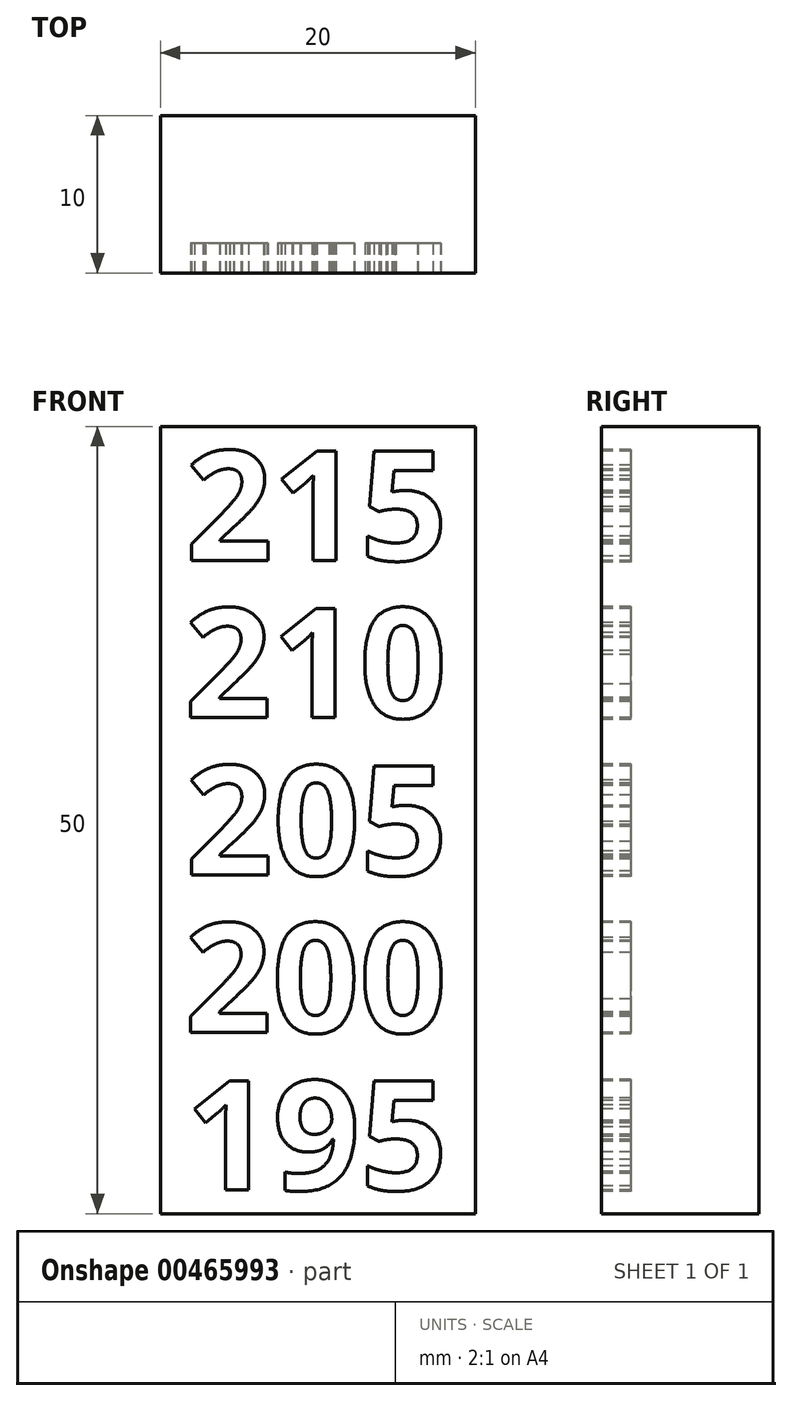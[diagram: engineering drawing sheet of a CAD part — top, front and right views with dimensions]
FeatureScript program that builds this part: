
annotation { "Feature Type Name" : "Feature", "Feature Type Description" : "" }
export const myFeature = defineFeature(function(context is Context, id is Id, definition is map)
    precondition{}
    {
        {
            var Q0;
            Q0=qCreatedBy(makeId("Top.planeOp"),FACE);
            var sketch = newSketch(context, id + "F0", { "sketchPlane" : qUnion([Q0])});
            skLineSegment(sketch, "E0.bottom", {"start": v(10, -5) * mm, "end": v(-10, -5) * mm});
            skLineSegment(sketch, "E0.top", {"start": v(10, 5) * mm, "end": v(-10, 5) * mm});
            skLineSegment(sketch, "E0.left", {"start": v(10, -5) * mm, "end": v(10, 5) * mm});
            skLineSegment(sketch, "E0.right", {"start": v(-10, -5) * mm, "end": v(-10, 5) * mm});
            skPoint(sketch, "E0.middle", {"position": v(0, 0) * mm});
            skSolve(sketch);
        }
        {
            var Q0;
            Q0=makeQuery(id+"F0.imprint","IMPRINT",FACE,{"disambiguationData":[TD([[makeQuery(id+"F0.imprint","IMPRINT",EDGE,{"derivedFrom":sQuery(id+"F0.wireOp",EDGE,"E0.bottom")}),-1.0]])]});
            extrude(context, id + "F1", {"entities" : qUnion([Q0]), "depth" : 50 * mm});
        }
        {
            var Q0;
            Q0=makeQuery(id+"F1.opExtrude","SWEPT_FACE",FACE,{"disambiguationData":[OSD([sQuery(id+"F0.wireOp",EDGE,"E0.bottom")])]});
            var sketch = newSketch(context, id + "F2", { "sketchPlane" : qUnion([Q0])});
            skLineSegment(sketch, "E1.bottom", {"start": v(-10, 50) * mm, "end": v(10, 50) * mm});
            skLineSegment(sketch, "E1.top", {"start": v(-10, 40) * mm, "end": v(10, 40) * mm});
            skLineSegment(sketch, "E1.left", {"start": v(-10, 50) * mm, "end": v(-10, 40) * mm});
            skLineSegment(sketch, "E1.right", {"start": v(10, 50) * mm, "end": v(10, 40) * mm});
            skLineSegment(sketch, "E2.bottom", {"start": v(10, 40) * mm, "end": v(-10, 40) * mm});
            skLineSegment(sketch, "E2.top", {"start": v(10, 30) * mm, "end": v(-10, 30) * mm});
            skLineSegment(sketch, "E2.left", {"start": v(10, 40) * mm, "end": v(10, 30) * mm});
            skLineSegment(sketch, "E2.right", {"start": v(-10, 40) * mm, "end": v(-10, 30) * mm});
            skLineSegment(sketch, "E3.bottom", {"start": v(-10, 30) * mm, "end": v(10, 30) * mm});
            skLineSegment(sketch, "E3.top", {"start": v(-10, 20) * mm, "end": v(10, 20) * mm});
            skLineSegment(sketch, "E3.left", {"start": v(-10, 30) * mm, "end": v(-10, 20) * mm});
            skLineSegment(sketch, "E3.right", {"start": v(10, 30) * mm, "end": v(10, 20) * mm});
            skLineSegment(sketch, "E4.bottom", {"start": v(10, 20) * mm, "end": v(-10, 20) * mm});
            skLineSegment(sketch, "E4.top", {"start": v(10, 10) * mm, "end": v(-10, 10) * mm});
            skLineSegment(sketch, "E4.left", {"start": v(10, 20) * mm, "end": v(10, 10) * mm});
            skLineSegment(sketch, "E4.right", {"start": v(-10, 20) * mm, "end": v(-10, 10) * mm});
            skLineSegment(sketch, "E5.bottom", {"start": v(-10, 10) * mm, "end": v(10, 10) * mm});
            skLineSegment(sketch, "E5.top", {"start": v(-10, 0) * mm, "end": v(10, 0) * mm});
            skLineSegment(sketch, "E5.left", {"start": v(-10, 10) * mm, "end": v(-10, 0) * mm});
            skLineSegment(sketch, "E5.right", {"start": v(10, 10) * mm, "end": v(10, 0) * mm});
            skPoint(sketch, "E6", {"position": v(0, 5) * mm});
            skPoint(sketch, "E7", {"position": v(0, 15) * mm});
            skPoint(sketch, "E8", {"position": v(0, 25) * mm});
            skPoint(sketch, "E9", {"position": v(0, 35) * mm});
            skPoint(sketch, "E10", {"position": v(0, 45) * mm});
            skLineSegment(sketch, "E11", {"start": v(-10, 45) * mm, "end": v(10, 45) * mm, "construction": true});
            skLineSegment(sketch, "E12", {"start": v(10, 35) * mm, "end": v(-10, 35) * mm, "construction": true});
            skLineSegment(sketch, "E13", {"start": v(-10, 25) * mm, "end": v(10, 25) * mm, "construction": true});
            skLineSegment(sketch, "E14", {"start": v(10, 15) * mm, "end": v(-10, 15) * mm, "construction": true});
            skLineSegment(sketch, "E15", {"start": v(-10, 5) * mm, "end": v(10, 5) * mm, "construction": true});
            skText(sketch, "E16", { "text": "195", "fontName": "OpenSans-Bold.ttf"});
            skText(sketch, "E17", { "text": "200", "fontName": "OpenSans-Bold.ttf"});
            skText(sketch, "E18", { "text": "210", "fontName": "OpenSans-Bold.ttf"});
            skText(sketch, "E19", { "text": "205", "fontName": "OpenSans-Bold.ttf"});
            skText(sketch, "E20", { "text": "215", "fontName": "OpenSans-Bold.ttf"});
            const initialGuessF2  = {"E16": [-0.00842, 0.0015, 1, 0, 0.007], "E17": [-0.00847, 0.0115, 1, 0, 0.007], "E18": [-0.00847, 0.0315, 1, 0, 0.007], "E19": [-0.00842, 0.0215, 1, 0, 0.007], "E20": [-0.00842, 0.0415, 1, 0, 0.007]};
            skSetInitialGuess(sketch, initialGuessF2);
            skSolve(sketch);
        }
        {
            var Q0;
            Q0=makeQuery(id+"F2.imprint","IMPRINT",FACE,{"disambiguationData":[TD([[makeQuery(id+"F2.imprint","IMPRINT",EDGE,{"derivedFrom":sQuery(id+"F2.wireOp",EDGE,"E20.sketch_text.stroke-0")}),-1.0]])]});
            var Q1;
            Q1=makeQuery(id+"F2.imprint","IMPRINT",FACE,{"disambiguationData":[TD([[makeQuery(id+"F2.imprint","IMPRINT",EDGE,{"derivedFrom":sQuery(id+"F2.wireOp",EDGE,"E20.sketch_text.stroke-24")}),-1.0]])]});
            var Q2;
            Q2=makeQuery(id+"F2.imprint","IMPRINT",FACE,{"disambiguationData":[TD([[makeQuery(id+"F2.imprint","IMPRINT",EDGE,{"derivedFrom":sQuery(id+"F2.wireOp",EDGE,"E20.sketch_text.stroke-34")}),-1.0]])]});
            var Q3;
            Q3=makeQuery(id+"F2.imprint","IMPRINT",FACE,{"disambiguationData":[TD([[makeQuery(id+"F2.imprint","IMPRINT",EDGE,{"derivedFrom":sQuery(id+"F2.wireOp",EDGE,"E18.sketch_text.stroke-34")}),-1.0]])]});
            var Q4;
            Q4=makeQuery(id+"F2.imprint","IMPRINT",FACE,{"disambiguationData":[TD([[makeQuery(id+"F2.imprint","IMPRINT",EDGE,{"derivedFrom":sQuery(id+"F2.wireOp",EDGE,"E18.sketch_text.stroke-24")}),-1.0]])]});
            var Q5;
            Q5=makeQuery(id+"F2.imprint","IMPRINT",FACE,{"disambiguationData":[TD([[makeQuery(id+"F2.imprint","IMPRINT",EDGE,{"derivedFrom":sQuery(id+"F2.wireOp",EDGE,"E18.sketch_text.stroke-0")}),-1.0]])]});
            var Q6;
            Q6=makeQuery(id+"F2.imprint","IMPRINT",FACE,{"disambiguationData":[TD([[makeQuery(id+"F2.imprint","IMPRINT",EDGE,{"derivedFrom":sQuery(id+"F2.wireOp",EDGE,"E19.sketch_text.stroke-0")}),-1.0]])]});
            var Q7;
            Q7=makeQuery(id+"F2.imprint","IMPRINT",FACE,{"disambiguationData":[TD([[makeQuery(id+"F2.imprint","IMPRINT",EDGE,{"derivedFrom":sQuery(id+"F2.wireOp",EDGE,"E19.sketch_text.stroke-24")}),-1.0]])]});
            var Q8;
            Q8=makeQuery(id+"F2.imprint","IMPRINT",FACE,{"disambiguationData":[TD([[makeQuery(id+"F2.imprint","IMPRINT",EDGE,{"derivedFrom":sQuery(id+"F2.wireOp",EDGE,"E19.sketch_text.stroke-40")}),-1.0]])]});
            var Q9;
            Q9=makeQuery(id+"F2.imprint","IMPRINT",FACE,{"disambiguationData":[TD([[makeQuery(id+"F2.imprint","IMPRINT",EDGE,{"derivedFrom":sQuery(id+"F2.wireOp",EDGE,"E17.sketch_text.stroke-0")}),-1.0]])]});
            var Q10;
            Q10=makeQuery(id+"F2.imprint","IMPRINT",FACE,{"disambiguationData":[TD([[makeQuery(id+"F2.imprint","IMPRINT",EDGE,{"derivedFrom":sQuery(id+"F2.wireOp",EDGE,"E17.sketch_text.stroke-24")}),-1.0]])]});
            var Q11;
            Q11=makeQuery(id+"F2.imprint","IMPRINT",FACE,{"disambiguationData":[TD([[makeQuery(id+"F2.imprint","IMPRINT",EDGE,{"derivedFrom":sQuery(id+"F2.wireOp",EDGE,"E17.sketch_text.stroke-40")}),-1.0]])]});
            var Q12;
            Q12=makeQuery(id+"F2.imprint","IMPRINT",FACE,{"disambiguationData":[TD([[makeQuery(id+"F2.imprint","IMPRINT",EDGE,{"derivedFrom":sQuery(id+"F2.wireOp",EDGE,"E16.sketch_text.stroke-0")}),-1.0]])]});
            var Q13;
            Q13=makeQuery(id+"F2.imprint","IMPRINT",FACE,{"disambiguationData":[TD([[makeQuery(id+"F2.imprint","IMPRINT",EDGE,{"derivedFrom":sQuery(id+"F2.wireOp",EDGE,"E16.sketch_text.stroke-10")}),-1.0]])]});
            var Q14;
            Q14=makeQuery(id+"F2.imprint","IMPRINT",FACE,{"disambiguationData":[TD([[makeQuery(id+"F2.imprint","IMPRINT",EDGE,{"derivedFrom":sQuery(id+"F2.wireOp",EDGE,"E16.sketch_text.stroke-36")}),-1.0]])]});
            extrude(context, id + "F3", {"entities" : qUnion([Q0, Q1, Q2, Q3, Q4, Q5, Q6, Q7, Q8, Q9, Q10, Q11, Q12, Q13, Q14]), "operationType" : NewBodyOperationType.REMOVE, "oppositeDirection" : true, "depth" : 1.9 * mm});
        }
    });
